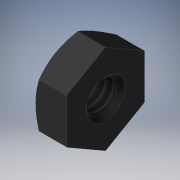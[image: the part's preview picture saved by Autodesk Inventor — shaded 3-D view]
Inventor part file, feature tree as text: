
AUTODESK INVENTOR PART (.ipt)
format: ipt  version: 2019 (Build 230136000, 136)  size: 155,136 bytes
history: native  units: mm
features: other x14, sketch x3, revolve x2, thread x1, extrude x1
ambient origin geometry x8: Origin, YZ Plane, XZ Plane, XY Plane, X Axis, Y Axis, Z Axis, Center Point
bodies: Solid1 (feature_tree)
feature tree (21):
  revolve  "Revolution1"  Angle=360.0deg
  revolve  "Revolution2"  [1 undecoded]
  thread  "Thread1"  [1 undecoded]
  extrude  "Extrusion1"  [1 undecoded]
  other  "cp_XY"
  other  "cp_YZ"
  other  "cp_ZX"
  other  "cp_X"
  other  "cp_Y"
  other  "cp_Z"
  other  "cp_Center"
  other  "nut_to_screw_XY"
  other  "nut_to_screw_YZ"
  other  "nut_to_screw_ZX"
  other  "nut_to_screw_X"
  other  "nut_to_screw_Y"
  other  "nut_to_screw_Z"
  other  "nut_to_screw_Center"
  sketch  "Sketch_1"  dims[d0=360.0deg d1=360.0deg]
  sketch  "Sketch_2"  dims[d2=1.167mm d3=0.0mm d4=1.6mm d5=0.0mm d6=0.0mm]
  sketch  "Sketch_3"
note: 3 required parameter values undecoded (feature->parameter linkage not recoverable at this tier; creation-order binding heuristic only, values carry confidence <= 0.55)